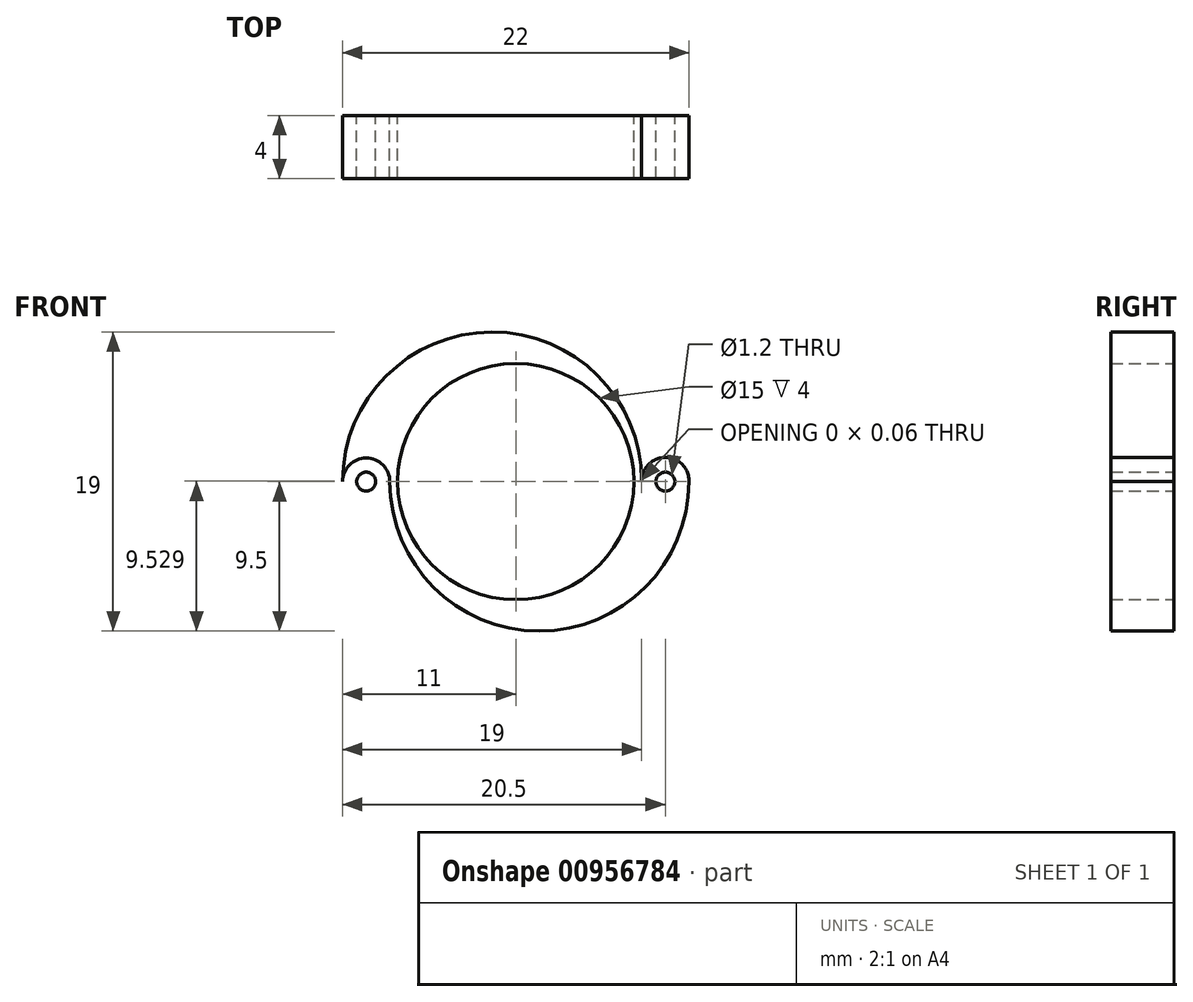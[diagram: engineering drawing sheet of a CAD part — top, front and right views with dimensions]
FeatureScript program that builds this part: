
annotation { "Feature Type Name" : "Feature", "Feature Type Description" : "" }
export const myFeature = defineFeature(function(context is Context, id is Id, definition is map)
    precondition{}
    {
        {
            var Q0;
            Q0=qCreatedBy(makeId("Front.planeOp"),FACE);
            var sketch = newSketch(context, id + "F0", { "sketchPlane" : qUnion([Q0])});
            skLineSegment(sketch, "E0", {"start": v(8, 0) * mm, "end": v(8, 0) * mm});
            skLineSegment(sketch, "E1", {"start": v(11, 0) * mm, "end": v(11, 0) * mm});
            skPoint(sketch, "E2.center.orphan", {"position": v(-9.5, 0) * mm});
            skArc(sketch, "E3", {"start": v(-8, 0) * mm, "mid": v(-9.5, 1.5) * mm, "end": v(-11, 0) * mm});
            skArc(sketch, "E4", {"start": v(8, 0) * mm, "mid": v(8, 0.03) * mm, "end": v(8, 0.06) * mm});
            skPoint(sketch, "E5.center.orphan", {"position": v(9.5, 0) * mm});
            skPoint(sketch, "E6.center.orphan", {"position": v(-1.5, 0) * mm});
            skArc(sketch, "E7", {"start": v(8, 0) * mm, "mid": v(-1.5, 9.5) * mm, "end": v(-11, 0) * mm});
            skCircle(sketch, "E8", {"center": v(-9.5, 0) * mm, "radius": 0.6 * mm});
            skPoint(sketch, "E9.1.0", {"position": v(1.5, 0) * mm});
            skLineSegment(sketch, "E9.1.2", {"start": v(-8, 0) * mm, "end": v(-8, 0) * mm});
            skPoint(sketch, "E9.1.4", {"position": v(9.5, 0) * mm});
            skArc(sketch, "E9.1.5", {"start": v(-8, 0) * mm, "mid": v(1.5, -9.5) * mm, "end": v(11, 0) * mm});
            skCircle(sketch, "E9.1.6", {"center": v(9.5, 0) * mm, "radius": 0.6 * mm});
            skLineSegment(sketch, "E9.1.7", {"start": v(-8, 0) * mm, "end": v(-8, 0) * mm});
            skArc(sketch, "E10", {"start": v(11, 0) * mm, "mid": v(9.5, 1.53) * mm, "end": v(8, 0) * mm});
            skCircle(sketch, "E11", {"center": v(0, 0) * mm, "radius": 7.5 * mm});
            skSolve(sketch);
        }
        {
            var Q0;
            Q0=qSketchRegion(id+"F0",true);
            extrude(context, id + "F1", {"entities" : qUnion([Q0]), "depth" : 4 * mm, "offsetDistance" : 25 * mm});
        }
    });
